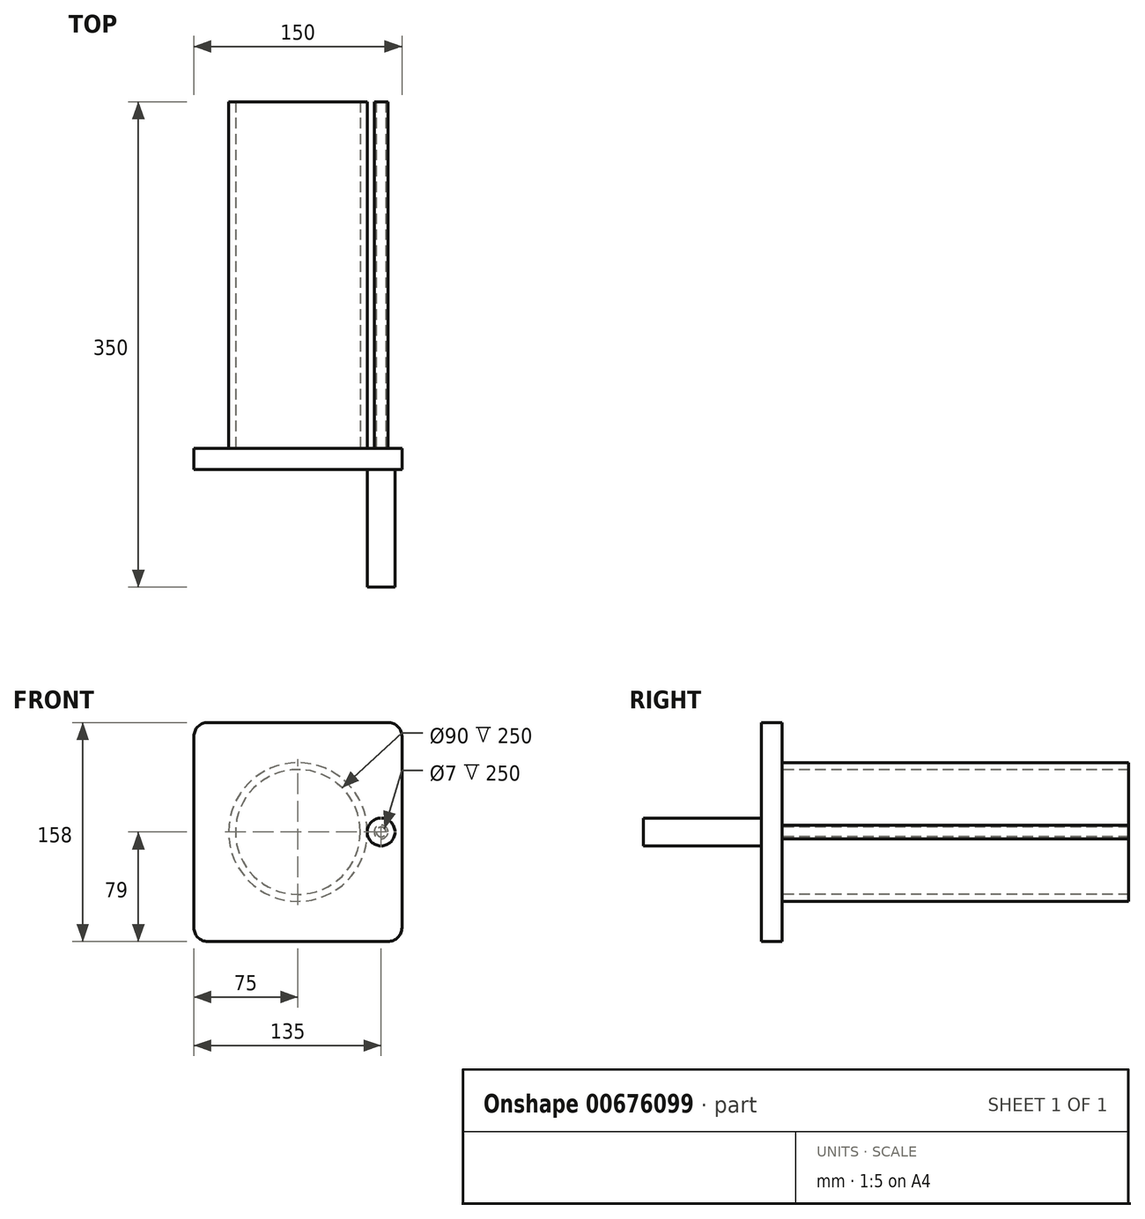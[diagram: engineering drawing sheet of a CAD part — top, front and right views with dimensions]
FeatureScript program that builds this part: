
annotation { "Feature Type Name" : "Feature", "Feature Type Description" : "" }
export const myFeature = defineFeature(function(context is Context, id is Id, definition is map)
    precondition{}
    {
        {
            var Q0;
            Q0=qCreatedBy(makeId("Front.planeOp"),FACE);
            var sketch = newSketch(context, id + "F0", { "sketchPlane" : qUnion([Q0])});
            skLineSegment(sketch, "E0.bottom", {"start": v(75, 79) * mm, "end": v(-75, 79) * mm});
            skLineSegment(sketch, "E0.top", {"start": v(75, -79) * mm, "end": v(-75, -79) * mm});
            skLineSegment(sketch, "E0.left", {"start": v(75, 79) * mm, "end": v(75, -79) * mm});
            skLineSegment(sketch, "E0.right", {"start": v(-75, 79) * mm, "end": v(-75, -79) * mm});
            skPoint(sketch, "E0.middle", {"position": v(0, 0) * mm});
            skSolve(sketch);
        }
        {
            var Q0;
            Q0 = qSketchRegion(id + "F0", true);
            extrude(context, id + "F1", {"entities" : qUnion([Q0]), "depth" : 15 * mm, "offsetDistance" : 25 * mm});
        }
        {
            var Q0;
            Q0=qCreatedBy(makeId("Front.planeOp"),FACE);
            var sketch = newSketch(context, id + "F2", { "sketchPlane" : qUnion([Q0])});
            skCircle(sketch, "E1", {"center": v(0, 0) * mm, "radius": 50 * mm});
            skCircle(sketch, "E2", {"center": v(0, 0) * mm, "radius": 45 * mm});
            skSolve(sketch);
        }
        {
            var Q0;
            Q0 = qSketchRegion(id + "F2", true);
            extrude(context, id + "F3", {"entities" : qUnion([Q0]), "operationType" : NewBodyOperationType.ADD, "oppositeDirection" : true, "depth" : 250 * mm, "offsetDistance" : 25 * mm});
        }
        {
            var Q0;
            Q0=qCreatedBy(makeId("Front.planeOp"),FACE);
            var sketch = newSketch(context, id + "F4", { "sketchPlane" : qUnion([Q0])});
            skCircle(sketch, "E3", {"center": v(60, 0) * mm, "radius": 5 * mm});
            skCircle(sketch, "E4", {"center": v(60, 0) * mm, "radius": 3.5 * mm});
            skSolve(sketch);
        }
        {
            var Q0;
            Q0 = qSketchRegion(id + "F4", true);
            extrude(context, id + "F5", {"entities" : qUnion([Q0]), "operationType" : NewBodyOperationType.ADD, "oppositeDirection" : true, "depth" : 250 * mm, "offsetDistance" : 25 * mm});
        }
        {
            var Q0;
            Q0=makeQuery(id+"F1.opExtrude","SWEPT_EDGE",EDGE,{"disambiguationData":[OSD([sQuery(id+"F0.wireOp",EDGE,"E0.bottom"),sQuery(id+"F0.wireOp",EDGE,"E0.left")])]});
            var Q1;
            Q1=makeQuery(id+"F1.opExtrude","SWEPT_EDGE",EDGE,{"disambiguationData":[OSD([sQuery(id+"F0.wireOp",EDGE,"E0.bottom"),sQuery(id+"F0.wireOp",EDGE,"E0.right")])]});
            var Q2;
            Q2=makeQuery(id+"F1.opExtrude","SWEPT_EDGE",EDGE,{"disambiguationData":[OSD([sQuery(id+"F0.wireOp",EDGE,"E0.top"),sQuery(id+"F0.wireOp",EDGE,"E0.right")])]});
            var Q3;
            Q3=makeQuery(id+"F1.opExtrude","SWEPT_EDGE",EDGE,{"disambiguationData":[OSD([sQuery(id+"F0.wireOp",EDGE,"E0.top"),sQuery(id+"F0.wireOp",EDGE,"E0.left")])]});
            fillet(context, id + "F6", {"entities" : qUnion([Q0, Q1, Q2, Q3]), "radius" : 10 * mm, "tangentPropagation" : true, "allowEdgeOverflow" : false});
        }
        {
            var Q0;
            Q0=qCreatedBy(makeId("Front.planeOp"),FACE);
            var sketch = newSketch(context, id + "F7", { "sketchPlane" : qUnion([Q0])});
            skCircle(sketch, "E5", {"center": v(60, 0) * mm, "radius": 10 * mm});
            skSolve(sketch);
        }
        {
            var Q0;
            Q0 = qSketchRegion(id + "F7", true);
            extrude(context, id + "F8", {"entities" : qUnion([Q0]), "operationType" : NewBodyOperationType.ADD, "depth" : 100 * mm, "offsetDistance" : 25 * mm});
        }
    });
